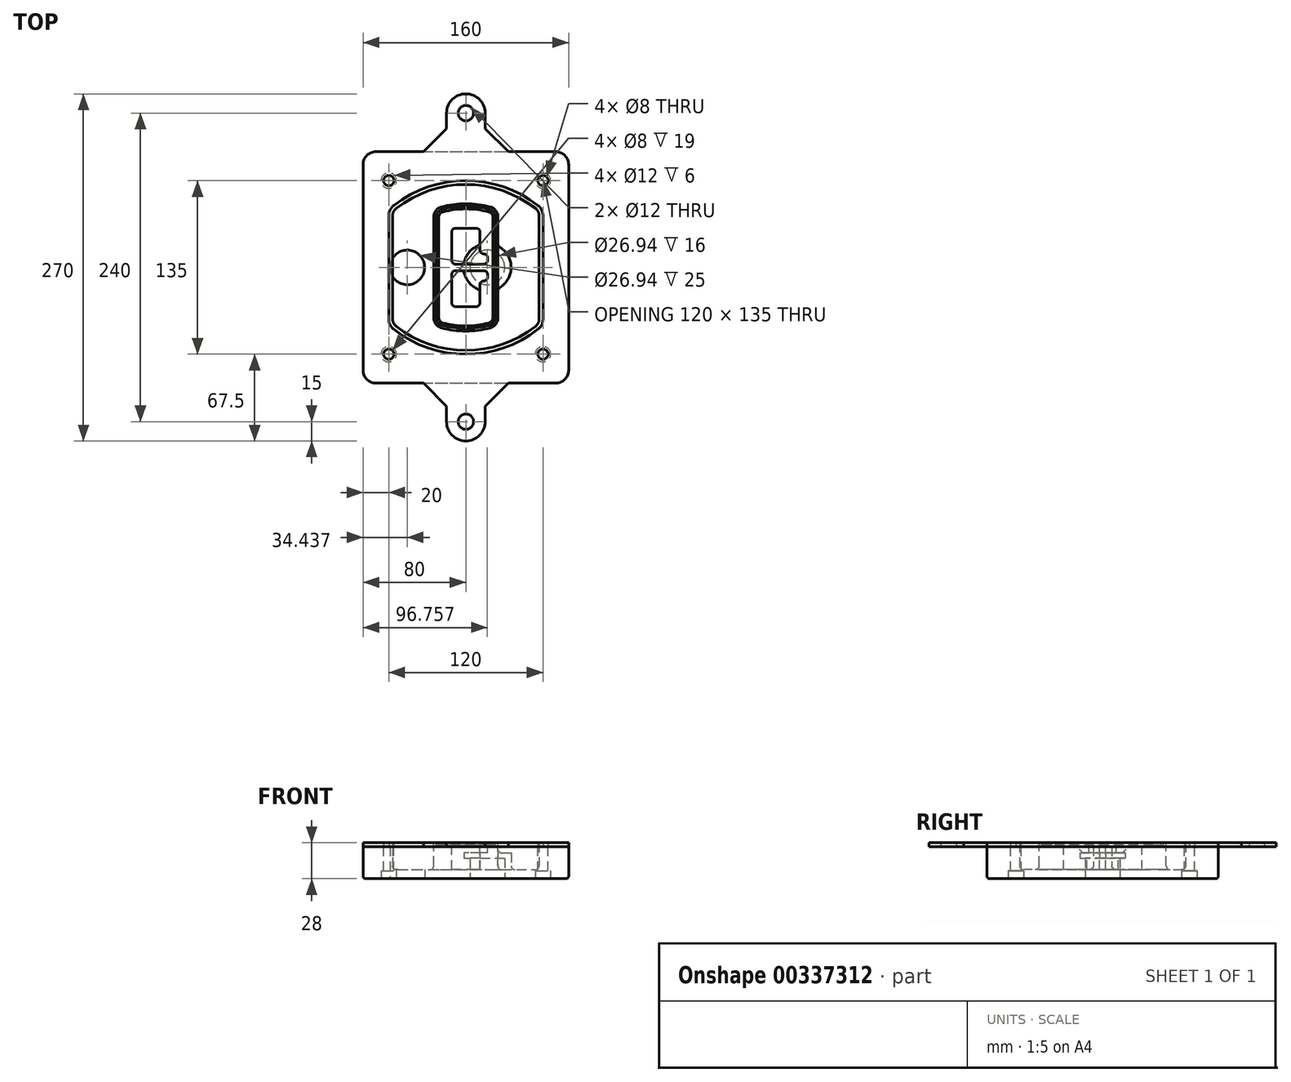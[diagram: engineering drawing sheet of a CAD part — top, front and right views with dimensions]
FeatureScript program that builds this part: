
annotation { "Feature Type Name" : "Feature", "Feature Type Description" : "" }
export const myFeature = defineFeature(function(context is Context, id is Id, definition is map)
    precondition{}
    {
        {
            var Q0;
            Q0=qCreatedBy(makeId("Top.planeOp"),FACE);
            var sketch = newSketch(context, id + "F0", { "sketchPlane" : qUnion([Q0])});
            skPoint(sketch, "E0.rect.middle", {"position": v(0, 0) * mm});
            skLineSegment(sketch, "E1.bottom", {"start": v(-70, -90) * mm, "end": v(70, -90) * mm});
            skLineSegment(sketch, "E1.top", {"start": v(-70, 90) * mm, "end": v(70, 90) * mm});
            skLineSegment(sketch, "E1.left", {"start": v(-80, -80) * mm, "end": v(-80, 80) * mm});
            skLineSegment(sketch, "E1.right", {"start": v(80, -80) * mm, "end": v(80, 80) * mm});
            skLineSegment(sketch, "E2", {"start": v(-80, 90) * mm, "end": v(80, -90) * mm, "construction": true});
            skLineSegment(sketch, "E3", {"start": v(80, 90) * mm, "end": v(-80, -90) * mm, "construction": true});
            skCircle(sketch, "E4", {"center": v(-60, 67.5) * mm, "radius": 4 * mm});
            skCircle(sketch, "E5", {"center": v(60, 67.5) * mm, "radius": 4 * mm});
            skCircle(sketch, "E6", {"center": v(60, -67.5) * mm, "radius": 4 * mm});
            skCircle(sketch, "E7", {"center": v(-60, -67.5) * mm, "radius": 4 * mm});
            skLineSegment(sketch, "E8", {"start": v(-60, 67.5) * mm, "end": v(60, 67.5) * mm, "construction": true});
            skLineSegment(sketch, "E9", {"start": v(60, 67.5) * mm, "end": v(60, -67.5) * mm, "construction": true});
            skLineSegment(sketch, "E10", {"start": v(60, -67.5) * mm, "end": v(-60, -67.5) * mm, "construction": true});
            skLineSegment(sketch, "E11", {"start": v(-60, -67.5) * mm, "end": v(-60, 67.5) * mm, "construction": true});
            skLineSegment(sketch, "E12", {"start": v(-60, 40.3) * mm, "end": v(-60, -40.3) * mm});
            skLineSegment(sketch, "E13", {"start": v(60, 40.3) * mm, "end": v(60, -40.3) * mm});
            skArc(sketch, "E14", {"start": v(56.15, 48.18) * mm, "mid": v(0, 67.5) * mm, "end": v(-56.15, 48.18) * mm});
            skArc(sketch, "E15", {"start": v(-56.15, -48.18) * mm, "mid": v(0, -67.5) * mm, "end": v(56.15, -48.18) * mm});
            skLineSegment(sketch, "E16", {"start": v(-60, 0) * mm, "end": v(60, 0) * mm, "construction": true});
            skPoint(sketch, "E17.visualSharp", {"position": v(-60, -45) * mm});
            skArc(sketch, "E17.filletArc", {"start": v(-60, -40.3) * mm, "mid": v(-58.99, -44.68) * mm, "end": v(-56.15, -48.18) * mm});
            skPoint(sketch, "E18.visualSharp", {"position": v(-60, 45) * mm});
            skArc(sketch, "E18.filletArc", {"start": v(-56.15, 48.18) * mm, "mid": v(-58.99, 44.68) * mm, "end": v(-60, 40.3) * mm});
            skPoint(sketch, "E19.visualSharp", {"position": v(60, 45) * mm});
            skArc(sketch, "E19.filletArc", {"start": v(60, 40.3) * mm, "mid": v(58.99, 44.68) * mm, "end": v(56.15, 48.18) * mm});
            skPoint(sketch, "E20.visualSharp", {"position": v(60, -45) * mm});
            skArc(sketch, "E20.filletArc", {"start": v(56.15, -48.18) * mm, "mid": v(58.99, -44.68) * mm, "end": v(60, -40.3) * mm});
            skPoint(sketch, "E21.visualSharp", {"position": v(-80, 90) * mm});
            skArc(sketch, "E21.filletArc", {"start": v(-70, 90) * mm, "mid": v(-77.07, 87.07) * mm, "end": v(-80, 80) * mm});
            skPoint(sketch, "E22.visualSharp", {"position": v(80, 90) * mm});
            skArc(sketch, "E22.filletArc", {"start": v(80, 80) * mm, "mid": v(77.07, 87.07) * mm, "end": v(70, 90) * mm});
            skPoint(sketch, "E23.visualSharp", {"position": v(80, -90) * mm});
            skArc(sketch, "E23.filletArc", {"start": v(70, -90) * mm, "mid": v(77.07, -87.07) * mm, "end": v(80, -80) * mm});
            skPoint(sketch, "E24.visualSharp", {"position": v(-80, -90) * mm});
            skArc(sketch, "E24.filletArc", {"start": v(-80, -80) * mm, "mid": v(-77.07, -87.07) * mm, "end": v(-70, -90) * mm});
            skArc(sketch, "E25.0", {"start": v(57, 40.3) * mm, "mid": v(56.3, 43.36) * mm, "end": v(54.3, 45.81) * mm});
            skLineSegment(sketch, "E25.1", {"start": v(57, 40.3) * mm, "end": v(57, -40.3) * mm});
            skArc(sketch, "E25.2", {"start": v(54.3, -45.81) * mm, "mid": v(56.3, -43.36) * mm, "end": v(57, -40.3) * mm});
            skArc(sketch, "E25.3", {"start": v(-54.3, -45.81) * mm, "mid": v(0, -64.5) * mm, "end": v(54.3, -45.81) * mm});
            skArc(sketch, "E25.4", {"start": v(-57, -40.3) * mm, "mid": v(-56.3, -43.36) * mm, "end": v(-54.3, -45.81) * mm});
            skArc(sketch, "E25.5", {"start": v(54.3, 45.81) * mm, "mid": v(0, 64.5) * mm, "end": v(-54.3, 45.81) * mm});
            skLineSegment(sketch, "E25.6", {"start": v(-57, 40.3) * mm, "end": v(-57, -40.3) * mm});
            skArc(sketch, "E25.7", {"start": v(-54.3, 45.81) * mm, "mid": v(-56.3, 43.36) * mm, "end": v(-57, 40.3) * mm});
            skArc(sketch, "E26.0", {"start": v(-58.62, 51.33) * mm, "mid": v(-62.58, 46.43) * mm, "end": v(-64, 40.3) * mm});
            skArc(sketch, "E26.1", {"start": v(58.62, 51.33) * mm, "mid": v(0, 71.5) * mm, "end": v(-58.62, 51.33) * mm});
            skArc(sketch, "E26.2", {"start": v(64, 40.3) * mm, "mid": v(62.58, 46.43) * mm, "end": v(58.62, 51.33) * mm});
            skLineSegment(sketch, "E26.3", {"start": v(64, 40.3) * mm, "end": v(64, -40.3) * mm});
            skArc(sketch, "E26.4", {"start": v(58.62, -51.33) * mm, "mid": v(62.58, -46.43) * mm, "end": v(64, -40.3) * mm});
            skLineSegment(sketch, "E26.5", {"start": v(-64, 40.3) * mm, "end": v(-64, -40.3) * mm});
            skArc(sketch, "E26.6", {"start": v(-58.62, -51.33) * mm, "mid": v(0, -71.5) * mm, "end": v(58.62, -51.33) * mm});
            skArc(sketch, "E26.7", {"start": v(-64, -40.3) * mm, "mid": v(-62.58, -46.43) * mm, "end": v(-58.62, -51.33) * mm});
            skSolve(sketch);
        }
        {
            var Q0;
            Q0=makeQuery(id+"F0.imprint","IMPRINT",FACE,{"disambiguationData":[TD([[makeQuery(id+"F0.imprint","IMPRINT",EDGE,{"derivedFrom":sQuery(id+"F0.wireOp",EDGE,"E1.bottom")}),1.0]])]});
            var Q1;
            Q1=makeQuery(id+"F0.imprint","IMPRINT",FACE,{"disambiguationData":[TD([[makeQuery(id+"F0.imprint","IMPRINT",EDGE,{"derivedFrom":sQuery(id+"F0.wireOp",EDGE,"E12")}),1.0]])]});
            var Q2;
            Q2=makeQuery(id+"F0.imprint","IMPRINT",FACE,{"disambiguationData":[TD([[makeQuery(id+"F0.imprint","IMPRINT",EDGE,{"derivedFrom":sQuery(id+"F0.wireOp",EDGE,"E25.0")}),1.0]])]});
            var Q3;
            Q3=makeQuery(id+"F0.imprint","IMPRINT",FACE,{"disambiguationData":[TD([[makeQuery(id+"F0.imprint","IMPRINT",EDGE,{"derivedFrom":sQuery(id+"F0.wireOp",EDGE,"E12")}),-1.0]])]});
            extrude(context, id + "F1", {"entities" : qUnion([Q0, Q1, Q2, Q3]), "oppositeDirection" : true, "depth" : 25 * mm});
        }
        {
            var Q0;
            Q0=makeQuery(id+"F0.imprint","IMPRINT",FACE,{"disambiguationData":[TD([[makeQuery(id+"F0.imprint","IMPRINT",EDGE,{"derivedFrom":sQuery(id+"F0.wireOp",EDGE,"E12")}),1.0]])]});
            extrude(context, id + "F2", {"entities" : qUnion([Q0]), "operationType" : NewBodyOperationType.ADD, "depth" : 3 * mm});
        }
        {
            var Q0;
            Q0=makeQuery(id+"F0.imprint","IMPRINT",FACE,{"disambiguationData":[TD([[makeQuery(id+"F0.imprint","IMPRINT",EDGE,{"derivedFrom":sQuery(id+"F0.wireOp",EDGE,"E25.0")}),1.0]])]});
            extrude(context, id + "F3", {"entities" : qUnion([Q0]), "operationType" : NewBodyOperationType.REMOVE, "oppositeDirection" : true, "depth" : 18 * mm});
        }
        {
            var Q0;
            Q0=makeQuery(id+"F2.opExtrude","CAP_FACE",FACE,{"disambiguationData":[OSD([sQuery(id+"F0.wireOp",EDGE,"E12"),sQuery(id+"F0.wireOp",EDGE,"E13"),sQuery(id+"F0.wireOp",EDGE,"E14"),sQuery(id+"F0.wireOp",EDGE,"E15"),sQuery(id+"F0.wireOp",EDGE,"E17.filletArc"),sQuery(id+"F0.wireOp",EDGE,"E18.filletArc"),sQuery(id+"F0.wireOp",EDGE,"E19.filletArc"),sQuery(id+"F0.wireOp",EDGE,"E20.filletArc"),sQuery(id+"F0.wireOp",EDGE,"E25.0"),sQuery(id+"F0.wireOp",EDGE,"E25.1"),sQuery(id+"F0.wireOp",EDGE,"E25.2"),sQuery(id+"F0.wireOp",EDGE,"E25.3"),sQuery(id+"F0.wireOp",EDGE,"E25.4"),sQuery(id+"F0.wireOp",EDGE,"E25.5"),sQuery(id+"F0.wireOp",EDGE,"E25.6"),sQuery(id+"F0.wireOp",EDGE,"E25.7")])],"isStart":false});
            var sketch = newSketch(context, id + "F4", { "sketchPlane" : qUnion([Q0])});
            skArc(sketch, "E27.0", {"start": v(-19.08, -46.97) * mm, "mid": v(0, -49.5) * mm, "end": v(19.08, -46.97) * mm});
            skArc(sketch, "E28.0", {"start": v(19.08, 46.97) * mm, "mid": v(0, 49.5) * mm, "end": v(-19.08, 46.97) * mm});
            skLineSegment(sketch, "E29", {"start": v(-25, 39.25) * mm, "end": v(-25, -39.25) * mm});
            skLineSegment(sketch, "E30", {"start": v(25, 39.25) * mm, "end": v(25, -39.25) * mm});
            skLineSegment(sketch, "E31", {"start": v(-25, 45.1) * mm, "end": v(25, 45.1) * mm, "construction": true});
            skLineSegment(sketch, "E32", {"start": v(-25, -45.1) * mm, "end": v(25, -45.1) * mm, "construction": true});
            skPoint(sketch, "E33.visualSharp", {"position": v(-25, 45.1) * mm});
            skArc(sketch, "E33.filletArc", {"start": v(-19.08, 46.97) * mm, "mid": v(-23.35, 44.11) * mm, "end": v(-25, 39.25) * mm});
            skPoint(sketch, "E34.visualSharp", {"position": v(25, 45.1) * mm});
            skArc(sketch, "E34.filletArc", {"start": v(25, 39.25) * mm, "mid": v(23.35, 44.11) * mm, "end": v(19.08, 46.97) * mm});
            skPoint(sketch, "E35.visualSharp", {"position": v(25, -45.1) * mm});
            skArc(sketch, "E35.filletArc", {"start": v(19.08, -46.97) * mm, "mid": v(23.35, -44.11) * mm, "end": v(25, -39.25) * mm});
            skPoint(sketch, "E36.visualSharp", {"position": v(-25, -45.1) * mm});
            skArc(sketch, "E36.filletArc", {"start": v(-25, -39.25) * mm, "mid": v(-23.35, -44.11) * mm, "end": v(-19.08, -46.97) * mm});
            skArc(sketch, "E37.0", {"start": v(54.3, 45.81) * mm, "mid": v(0, 64.5) * mm, "end": v(-54.3, 45.81) * mm});
            skArc(sketch, "E37.1", {"start": v(-54.3, 45.81) * mm, "mid": v(-56.3, 43.36) * mm, "end": v(-57, 40.3) * mm});
            skLineSegment(sketch, "E37.2", {"start": v(-57, 40.3) * mm, "end": v(-57, -40.3) * mm});
            skArc(sketch, "E37.3", {"start": v(-57, -40.3) * mm, "mid": v(-56.3, -43.36) * mm, "end": v(-54.3, -45.81) * mm});
            skArc(sketch, "E37.4", {"start": v(-54.3, -45.81) * mm, "mid": v(0, -64.5) * mm, "end": v(54.3, -45.81) * mm});
            skArc(sketch, "E37.5", {"start": v(54.3, -45.81) * mm, "mid": v(56.3, -43.36) * mm, "end": v(57, -40.3) * mm});
            skLineSegment(sketch, "E37.6", {"start": v(57, 40.3) * mm, "end": v(57, -40.3) * mm});
            skArc(sketch, "E37.7", {"start": v(57, 40.3) * mm, "mid": v(56.3, 43.36) * mm, "end": v(54.3, 45.81) * mm});
            skLineSegment(sketch, "E38.0", {"start": v(23, 39.25) * mm, "end": v(23, -39.25) * mm});
            skArc(sketch, "E38.1", {"start": v(18.56, -45.04) * mm, "mid": v(21.76, -42.9) * mm, "end": v(23, -39.25) * mm});
            skArc(sketch, "E38.2", {"start": v(-18.56, -45.04) * mm, "mid": v(0, -47.5) * mm, "end": v(18.56, -45.04) * mm});
            skArc(sketch, "E38.3", {"start": v(-23, -39.25) * mm, "mid": v(-21.76, -42.9) * mm, "end": v(-18.56, -45.04) * mm});
            skLineSegment(sketch, "E38.4", {"start": v(-23, 39.25) * mm, "end": v(-23, -39.25) * mm});
            skArc(sketch, "E38.5", {"start": v(23, 39.25) * mm, "mid": v(21.76, 42.9) * mm, "end": v(18.56, 45.04) * mm});
            skArc(sketch, "E38.6", {"start": v(-18.56, 45.04) * mm, "mid": v(-21.76, 42.9) * mm, "end": v(-23, 39.25) * mm});
            skArc(sketch, "E38.7", {"start": v(18.56, 45.04) * mm, "mid": v(0, 47.5) * mm, "end": v(-18.56, 45.04) * mm});
            skArc(sketch, "E39.0", {"start": v(21, 39.25) * mm, "mid": v(20.18, 41.68) * mm, "end": v(18.04, 43.1) * mm});
            skLineSegment(sketch, "E39.1", {"start": v(21, 39.25) * mm, "end": v(21, -39.25) * mm});
            skArc(sketch, "E39.2", {"start": v(18.04, -43.1) * mm, "mid": v(20.18, -41.68) * mm, "end": v(21, -39.25) * mm});
            skArc(sketch, "E39.3", {"start": v(-18.04, -43.1) * mm, "mid": v(0, -45.5) * mm, "end": v(18.04, -43.1) * mm});
            skArc(sketch, "E39.4", {"start": v(-21, -39.25) * mm, "mid": v(-20.18, -41.68) * mm, "end": v(-18.04, -43.1) * mm});
            skArc(sketch, "E39.5", {"start": v(18.04, 43.1) * mm, "mid": v(0, 45.5) * mm, "end": v(-18.04, 43.1) * mm});
            skLineSegment(sketch, "E39.6", {"start": v(-21, 39.25) * mm, "end": v(-21, -39.25) * mm});
            skArc(sketch, "E39.7", {"start": v(-18.04, 43.1) * mm, "mid": v(-20.18, 41.68) * mm, "end": v(-21, 39.25) * mm});
            skLineSegment(sketch, "E40", {"start": v(-25, 0) * mm, "end": v(25, 0) * mm, "construction": true});
            skLineSegment(sketch, "E41", {"start": v(-11, 5.5) * mm, "end": v(-11, 27.5) * mm});
            skLineSegment(sketch, "E42", {"start": v(-8, 30.5) * mm, "end": v(8, 30.5) * mm});
            skLineSegment(sketch, "E43", {"start": v(11, 27.5) * mm, "end": v(11, 13.5) * mm});
            skLineSegment(sketch, "E44", {"start": v(14, 10.5) * mm, "end": v(14, 10.5) * mm});
            skLineSegment(sketch, "E45", {"start": v(17, 7.5) * mm, "end": v(17, 5.5) * mm});
            skLineSegment(sketch, "E46", {"start": v(14, 2.5) * mm, "end": v(-8, 2.5) * mm});
            skPoint(sketch, "E47.visualSharp", {"position": v(-11, 30.5) * mm});
            skArc(sketch, "E47.filletArc", {"start": v(-8, 30.5) * mm, "mid": v(-10.12, 29.62) * mm, "end": v(-11, 27.5) * mm});
            skPoint(sketch, "E48.visualSharp", {"position": v(11, 30.5) * mm});
            skArc(sketch, "E48.filletArc", {"start": v(11, 27.5) * mm, "mid": v(10.12, 29.62) * mm, "end": v(8, 30.5) * mm});
            skPoint(sketch, "E49.visualSharp", {"position": v(11, 10.5) * mm});
            skArc(sketch, "E49.filletArc", {"start": v(11, 13.5) * mm, "mid": v(11.88, 11.38) * mm, "end": v(14, 10.5) * mm});
            skPoint(sketch, "E50.visualSharp", {"position": v(17, 10.5) * mm});
            skArc(sketch, "E50.filletArc", {"start": v(17, 7.5) * mm, "mid": v(16.12, 9.62) * mm, "end": v(14, 10.5) * mm});
            skPoint(sketch, "E51.visualSharp", {"position": v(17, 2.5) * mm});
            skArc(sketch, "E51.filletArc", {"start": v(14, 2.5) * mm, "mid": v(16.12, 3.38) * mm, "end": v(17, 5.5) * mm});
            skPoint(sketch, "E52.visualSharp", {"position": v(-11, 2.5) * mm});
            skArc(sketch, "E52.filletArc", {"start": v(-11, 5.5) * mm, "mid": v(-10.12, 3.38) * mm, "end": v(-8, 2.5) * mm});
            skLineSegment(sketch, "E53.0.MirrorCS", {"start": v(14, -2.5) * mm, "end": v(-8, -2.5) * mm});
            skArc(sketch, "E54.0.MirrorCS", {"start": v(-11, -5.5) * mm, "mid": v(-10.12, -3.38) * mm, "end": v(-8, -2.5) * mm});
            skLineSegment(sketch, "E55.0.MirrorCS", {"start": v(-11, -5.5) * mm, "end": v(-11, -27.5) * mm});
            skArc(sketch, "E56.0.MirrorCS", {"start": v(-8, -30.5) * mm, "mid": v(-10.12, -29.62) * mm, "end": v(-11, -27.5) * mm});
            skLineSegment(sketch, "E57.0.MirrorCS", {"start": v(-8, -30.5) * mm, "end": v(8, -30.5) * mm});
            skArc(sketch, "E58.0.MirrorCS", {"start": v(11, -27.5) * mm, "mid": v(10.12, -29.62) * mm, "end": v(8, -30.5) * mm});
            skLineSegment(sketch, "E59.0.MirrorCS", {"start": v(11, -27.5) * mm, "end": v(11, -13.5) * mm});
            skArc(sketch, "E60.0.MirrorCS", {"start": v(11, -13.5) * mm, "mid": v(11.88, -11.38) * mm, "end": v(14, -10.5) * mm});
            skArc(sketch, "E61.0.MirrorCS", {"start": v(17, -7.5) * mm, "mid": v(16.12, -9.62) * mm, "end": v(14, -10.5) * mm});
            skLineSegment(sketch, "E62.0.MirrorCS", {"start": v(17, -7.5) * mm, "end": v(17, -5.5) * mm});
            skArc(sketch, "E63.0.MirrorCS", {"start": v(14, -2.5) * mm, "mid": v(16.12, -3.38) * mm, "end": v(17, -5.5) * mm});
            skSolve(sketch);
        }
        {
            var Q0;
            Q0=makeQuery(id+"F4.imprint","IMPRINT",FACE,{"disambiguationData":[TD([[makeQuery(id+"F4.imprint","IMPRINT",EDGE,{"derivedFrom":sQuery(id+"F4.wireOp",EDGE,"E27.0")}),1.0]])]});
            var Q1;
            Q1=makeQuery(id+"F4.imprint","IMPRINT",FACE,{"disambiguationData":[TD([[makeQuery(id+"F4.imprint","IMPRINT",EDGE,{"derivedFrom":sQuery(id+"F4.wireOp",EDGE,"E38.0")}),-1.0]])]});
            var Q2;
            Q2=makeQuery(id+"F4.imprint","IMPRINT",FACE,{"disambiguationData":[TD([[makeQuery(id+"F4.imprint","IMPRINT",EDGE,{"derivedFrom":sQuery(id+"F4.wireOp",EDGE,"E39.0")}),1.0]])]});
            extrude(context, id + "F5", {"entities" : qUnion([Q0, Q1, Q2]), "operationType" : NewBodyOperationType.ADD, "endBound" : BoundingType.UP_TO_NEXT, "oppositeDirection" : true, "depth" : 25 * mm});
        }
        {
            var Q0;
            Q0=makeQuery(id+"F4.imprint","IMPRINT",FACE,{"disambiguationData":[TD([[makeQuery(id+"F4.imprint","IMPRINT",EDGE,{"derivedFrom":sQuery(id+"F4.wireOp",EDGE,"E38.0")}),-1.0]])]});
            extrude(context, id + "F6", {"entities" : qUnion([Q0]), "operationType" : NewBodyOperationType.REMOVE, "oppositeDirection" : true, "depth" : 2 * mm});
        }
        {
            var Q0;
            Q0=makeQuery(id+"F1.opExtrude","CAP_FACE",FACE,{"disambiguationData":[OSD([sQuery(id+"F0.wireOp",EDGE,"E1.bottom"),sQuery(id+"F0.wireOp",EDGE,"E1.top"),sQuery(id+"F0.wireOp",EDGE,"E1.left"),sQuery(id+"F0.wireOp",EDGE,"E1.right"),sQuery(id+"F0.wireOp",EDGE,"E4"),sQuery(id+"F0.wireOp",EDGE,"E5"),sQuery(id+"F0.wireOp",EDGE,"E6"),sQuery(id+"F0.wireOp",EDGE,"E7"),sQuery(id+"F0.wireOp",EDGE,"E21.filletArc"),sQuery(id+"F0.wireOp",EDGE,"E22.filletArc"),sQuery(id+"F0.wireOp",EDGE,"E23.filletArc"),sQuery(id+"F0.wireOp",EDGE,"E24.filletArc")])],"isStart":false});
            var sketch = newSketch(context, id + "F7", { "sketchPlane" : qUnion([Q0])});
            skCircle(sketch, "E64", {"center": v(16.76, 0) * mm, "radius": 13.47 * mm});
            skCircle(sketch, "E65", {"center": v(-45.56, 0) * mm, "radius": 13.47 * mm});
            skLineSegment(sketch, "E66", {"start": v(80, 0) * mm, "end": v(-80, 0) * mm});
            skCircle(sketch, "E67", {"center": v(16.76, 0) * mm, "radius": 18.47 * mm});
            skCircle(sketch, "E68", {"center": v(60, -67.5) * mm, "radius": 6 * mm});
            skCircle(sketch, "E69", {"center": v(-60, -67.5) * mm, "radius": 6 * mm});
            skCircle(sketch, "E70", {"center": v(-60, 67.5) * mm, "radius": 6 * mm});
            skCircle(sketch, "E71", {"center": v(60, 67.5) * mm, "radius": 6 * mm});
            skSolve(sketch);
        }
        {
            var Q0;
            {var subQ1=sQuery(id+"F7.wireOp",EDGE,"E66");var subQ4=sQuery(id+"F7.wireOp",EDGE,"E64");var subQ6=makeQuery(id+"F7.imprint","INTERSECT",VERTEX,{"disambiguationData":[OD(0.0)],"derivedFrom":[subQ4,subQ1]});Q0=makeQuery(id+"F7.imprint","IMPRINT",FACE,{"disambiguationData":[TD([[makeQuery(id+"F7.imprint","IMPRINT",EDGE,{"disambiguationData":[TD([[subQ6,-1.0]])],"derivedFrom":subQ4}),-1.0]])]});}
            var Q1;
            {var subQ0=sQuery(id+"F7.wireOp",EDGE,"E66");var subQ1=sQuery(id+"F7.wireOp",EDGE,"E64");var subQ3=makeQuery(id+"F7.imprint","INTERSECT",VERTEX,{"disambiguationData":[OD(0.0)],"derivedFrom":[subQ1,subQ0]});Q1=makeQuery(id+"F7.imprint","IMPRINT",FACE,{"disambiguationData":[TD([[makeQuery(id+"F7.imprint","IMPRINT",EDGE,{"disambiguationData":[TD([[subQ3,-1.0]])],"derivedFrom":subQ1}),1.0]])]});}
            var Q2;
            {var subQ0=sQuery(id+"F7.wireOp",EDGE,"E66");var subQ1=sQuery(id+"F7.wireOp",EDGE,"E64");var subQ3=makeQuery(id+"F7.imprint","INTERSECT",VERTEX,{"disambiguationData":[OD(0.0)],"derivedFrom":[subQ1,subQ0]});Q2=makeQuery(id+"F7.imprint","IMPRINT",FACE,{"disambiguationData":[TD([[makeQuery(id+"F7.imprint","IMPRINT",EDGE,{"disambiguationData":[TD([[subQ3,1.0]])],"derivedFrom":subQ1}),1.0]])]});}
            var Q3;
            {var subQ1=sQuery(id+"F7.wireOp",EDGE,"E66");var subQ4=sQuery(id+"F7.wireOp",EDGE,"E64");var subQ6=makeQuery(id+"F7.imprint","INTERSECT",VERTEX,{"disambiguationData":[OD(0.0)],"derivedFrom":[subQ4,subQ1]});Q3=makeQuery(id+"F7.imprint","IMPRINT",FACE,{"disambiguationData":[TD([[makeQuery(id+"F7.imprint","IMPRINT",EDGE,{"disambiguationData":[TD([[subQ6,1.0]])],"derivedFrom":subQ4}),-1.0]])]});}
            extrude(context, id + "F8", {"entities" : qUnion([Q0, Q1, Q2, Q3]), "operationType" : NewBodyOperationType.ADD, "oppositeDirection" : true, "depth" : 20 * mm});
        }
        {
            var Q0;
            {var subQ0=sQuery(id+"F7.wireOp",EDGE,"E66");var subQ1=sQuery(id+"F7.wireOp",EDGE,"E64");var subQ3=makeQuery(id+"F7.imprint","INTERSECT",VERTEX,{"disambiguationData":[OD(0.0)],"derivedFrom":[subQ1,subQ0]});Q0=makeQuery(id+"F7.imprint","IMPRINT",FACE,{"disambiguationData":[TD([[makeQuery(id+"F7.imprint","IMPRINT",EDGE,{"disambiguationData":[TD([[subQ3,-1.0]])],"derivedFrom":subQ1}),1.0]])]});}
            var Q1;
            {var subQ0=sQuery(id+"F7.wireOp",EDGE,"E66");var subQ1=sQuery(id+"F7.wireOp",EDGE,"E64");var subQ3=makeQuery(id+"F7.imprint","INTERSECT",VERTEX,{"disambiguationData":[OD(0.0)],"derivedFrom":[subQ1,subQ0]});Q1=makeQuery(id+"F7.imprint","IMPRINT",FACE,{"disambiguationData":[TD([[makeQuery(id+"F7.imprint","IMPRINT",EDGE,{"disambiguationData":[TD([[subQ3,1.0]])],"derivedFrom":subQ1}),1.0]])]});}
            extrude(context, id + "F9", {"entities" : qUnion([Q0, Q1]), "operationType" : NewBodyOperationType.REMOVE, "oppositeDirection" : true, "depth" : 16 * mm});
        }
        {
            var Q0;
            {var subQ0=sQuery(id+"F7.wireOp",EDGE,"E66");var subQ1=sQuery(id+"F7.wireOp",EDGE,"E65");var subQ3=makeQuery(id+"F7.imprint","INTERSECT",VERTEX,{"disambiguationData":[OD(0.0)],"derivedFrom":[subQ1,subQ0]});Q0=makeQuery(id+"F7.imprint","IMPRINT",FACE,{"disambiguationData":[TD([[makeQuery(id+"F7.imprint","IMPRINT",EDGE,{"disambiguationData":[TD([[subQ3,-1.0]])],"derivedFrom":subQ1}),1.0]])]});}
            var Q1;
            {var subQ0=sQuery(id+"F7.wireOp",EDGE,"E66");var subQ1=sQuery(id+"F7.wireOp",EDGE,"E65");var subQ3=makeQuery(id+"F7.imprint","INTERSECT",VERTEX,{"disambiguationData":[OD(0.0)],"derivedFrom":[subQ1,subQ0]});Q1=makeQuery(id+"F7.imprint","IMPRINT",FACE,{"disambiguationData":[TD([[makeQuery(id+"F7.imprint","IMPRINT",EDGE,{"disambiguationData":[TD([[subQ3,1.0]])],"derivedFrom":subQ1}),1.0]])]});}
            extrude(context, id + "F10", {"entities" : qUnion([Q0, Q1]), "operationType" : NewBodyOperationType.REMOVE, "oppositeDirection" : true, "depth" : 25 * mm});
        }
        {
            var Q0;
            Q0=makeQuery(id+"F7.imprint","IMPRINT",FACE,{"disambiguationData":[TD([[makeQuery(id+"F7.imprint","IMPRINT",EDGE,{"derivedFrom":sQuery(id+"F7.wireOp",EDGE,"E68")}),1.0]])]});
            var Q1;
            Q1=makeQuery(id+"F7.imprint","IMPRINT",FACE,{"disambiguationData":[TD([[makeQuery(id+"F7.imprint","IMPRINT",EDGE,{"derivedFrom":makeQuery(id+"F1.opExtrude","CAP_EDGE",EDGE,{"disambiguationData":[OSD([sQuery(id+"F0.wireOp",EDGE,"E5")])],"isStart":false})}),-1.0]])]});
            var Q2;
            Q2=makeQuery(id+"F7.imprint","IMPRINT",FACE,{"disambiguationData":[TD([[makeQuery(id+"F7.imprint","IMPRINT",EDGE,{"derivedFrom":sQuery(id+"F7.wireOp",EDGE,"E69")}),1.0]])]});
            var Q3;
            Q3=makeQuery(id+"F7.imprint","IMPRINT",FACE,{"disambiguationData":[TD([[makeQuery(id+"F7.imprint","IMPRINT",EDGE,{"derivedFrom":makeQuery(id+"F1.opExtrude","CAP_EDGE",EDGE,{"disambiguationData":[OSD([sQuery(id+"F0.wireOp",EDGE,"E4")])],"isStart":false})}),-1.0]])]});
            var Q4;
            Q4=makeQuery(id+"F7.imprint","IMPRINT",FACE,{"disambiguationData":[TD([[makeQuery(id+"F7.imprint","IMPRINT",EDGE,{"derivedFrom":sQuery(id+"F7.wireOp",EDGE,"E70")}),1.0]])]});
            var Q5;
            Q5=makeQuery(id+"F7.imprint","IMPRINT",FACE,{"disambiguationData":[TD([[makeQuery(id+"F7.imprint","IMPRINT",EDGE,{"derivedFrom":makeQuery(id+"F1.opExtrude","CAP_EDGE",EDGE,{"disambiguationData":[OSD([sQuery(id+"F0.wireOp",EDGE,"E7")])],"isStart":false})}),-1.0]])]});
            var Q6;
            Q6=makeQuery(id+"F7.imprint","IMPRINT",FACE,{"disambiguationData":[TD([[makeQuery(id+"F7.imprint","IMPRINT",EDGE,{"derivedFrom":sQuery(id+"F7.wireOp",EDGE,"E71")}),1.0]])]});
            var Q7;
            Q7=makeQuery(id+"F7.imprint","IMPRINT",FACE,{"disambiguationData":[TD([[makeQuery(id+"F7.imprint","IMPRINT",EDGE,{"derivedFrom":makeQuery(id+"F1.opExtrude","CAP_EDGE",EDGE,{"disambiguationData":[OSD([sQuery(id+"F0.wireOp",EDGE,"E6")])],"isStart":false})}),-1.0]])]});
            extrude(context, id + "F11", {"entities" : qUnion([Q0, Q1, Q2, Q3, Q4, Q5, Q6, Q7]), "operationType" : NewBodyOperationType.REMOVE, "oppositeDirection" : true, "depth" : 6 * mm});
        }
        {
            var Q0;
            Q0=makeQuery(id+"F9.boolean.opBoolean","COPY",FACE,{"derivedFrom":makeQuery(id+"F9.opExtrude","CAP_FACE",FACE,{"disambiguationData":[OSD([sQuery(id+"F7.wireOp",EDGE,"E64")])],"isStart":false})});
            var sketch = newSketch(context, id + "F12", { "sketchPlane" : qUnion([Q0])});
            skArc(sketch, "E72.0", {"start": v(11, 17.55) * mm, "mid": v(2.57, 11.82) * mm, "end": v(-1.54, 2.5) * mm});
            skArc(sketch, "E72.1", {"start": v(-1.54, -2.5) * mm, "mid": v(2.57, -11.82) * mm, "end": v(11, -17.55) * mm});
            skLineSegment(sketch, "E73", {"start": v(-1.54, -2.5) * mm, "end": v(14, -2.5) * mm});
            skLineSegment(sketch, "E74.0", {"start": v(14, 2.5) * mm, "end": v(-1.54, 2.5) * mm});
            skArc(sketch, "E74.1", {"start": v(14, 2.5) * mm, "mid": v(16.12, 3.38) * mm, "end": v(17, 5.5) * mm});
            skLineSegment(sketch, "E74.2", {"start": v(17, 7.5) * mm, "end": v(17, 5.5) * mm});
            skArc(sketch, "E74.3", {"start": v(17, 7.5) * mm, "mid": v(16.12, 9.62) * mm, "end": v(14, 10.5) * mm});
            skArc(sketch, "E74.4", {"start": v(11, 13.5) * mm, "mid": v(11.88, 11.38) * mm, "end": v(14, 10.5) * mm});
            skLineSegment(sketch, "E74.5", {"start": v(11, 17.55) * mm, "end": v(11, 13.5) * mm});
            skLineSegment(sketch, "E74.7", {"start": v(14, -2.5) * mm, "end": v(-1.54, -2.5) * mm});
            skArc(sketch, "E74.8", {"start": v(14, -2.5) * mm, "mid": v(16.12, -3.38) * mm, "end": v(17, -5.5) * mm});
            skLineSegment(sketch, "E74.9", {"start": v(17, -7.5) * mm, "end": v(17, -5.5) * mm});
            skArc(sketch, "E74.10", {"start": v(17, -7.5) * mm, "mid": v(16.12, -9.62) * mm, "end": v(14, -10.5) * mm});
            skArc(sketch, "E74.11", {"start": v(11, -13.5) * mm, "mid": v(11.88, -11.38) * mm, "end": v(14, -10.5) * mm});
            skLineSegment(sketch, "E74.12", {"start": v(11, -17.55) * mm, "end": v(11, -13.5) * mm});
            skPoint(sketch, "E75.orphan", {"position": v(11, -27.5) * mm});
            skPoint(sketch, "E76.orphan", {"position": v(-8, -2.5) * mm});
            skPoint(sketch, "E77.orphan", {"position": v(-8, 2.5) * mm});
            skPoint(sketch, "E78.orphan", {"position": v(11, 27.5) * mm});
            skSolve(sketch);
        }
        {
            var Q0;
            {var subQ7=sQuery(id+"F12.wireOp",EDGE,"E72.0");var subQ14=sQuery(id+"F12.wireOp",EDGE,"E72.1");var subQ16=sQuery(id+"F12.wireOp",EDGE,"E74.1");var subQ18=sQuery(id+"F12.wireOp",EDGE,"E74.8");Q0=qUnion([makeQuery(id+"F12.imprint","IMPRINT",FACE,{"disambiguationData":[TD([[makeQuery(id+"F12.imprint","IMPRINT",EDGE,{"derivedFrom":subQ7}),1.0]])]}),makeQuery(id+"F12.imprint","IMPRINT",FACE,{"disambiguationData":[TD([[makeQuery(id+"F12.imprint","IMPRINT",EDGE,{"derivedFrom":subQ14}),1.0]])]}),makeQuery(id+"F12.imprint","IMPRINT",FACE,{"disambiguationData":[TD([[makeQuery(id+"F12.imprint","IMPRINT",EDGE,{"derivedFrom":subQ16}),1.0]])]}),makeQuery(id+"F12.imprint","IMPRINT",FACE,{"disambiguationData":[TD([[makeQuery(id+"F12.imprint","IMPRINT",EDGE,{"derivedFrom":subQ18}),-1.0]])]})]);}
            var Q1;
            Q1=makeQuery(id+"F5.boolean.opBoolean","SPLIT",FACE,{"disambiguationData":[TD([makeQuery(id+"F5.opExtrude","SWEPT_FACE",FACE,{"disambiguationData":[OSD([sQuery(id+"F4.wireOp",EDGE,"E41")])]})])],"derivedFrom":makeQuery(id+"F3.boolean.opBoolean","COPY",FACE,{"derivedFrom":makeQuery(id+"F3.opExtrude","CAP_FACE",FACE,{"disambiguationData":[OSD([sQuery(id+"F0.wireOp",EDGE,"E25.0"),sQuery(id+"F0.wireOp",EDGE,"E25.1"),sQuery(id+"F0.wireOp",EDGE,"E25.2"),sQuery(id+"F0.wireOp",EDGE,"E25.3"),sQuery(id+"F0.wireOp",EDGE,"E25.4"),sQuery(id+"F0.wireOp",EDGE,"E25.5"),sQuery(id+"F0.wireOp",EDGE,"E25.6"),sQuery(id+"F0.wireOp",EDGE,"E25.7")])],"isStart":false})})});
            extrude(context, id + "F13", {"entities" : qUnion([Q0]), "operationType" : NewBodyOperationType.REMOVE, "endBound" : BoundingType.UP_TO_SURFACE, "endBoundEntityFace" : qUnion([Q1]), "depth" : 25 * mm});
        }
        {
            var Q0;
            Q0=makeQuery(id+"F3.boolean.opBoolean","COPY",EDGE,{"derivedFrom":makeQuery(id+"F3.opExtrude","CAP_EDGE",EDGE,{"disambiguationData":[OSD([sQuery(id+"F0.wireOp",EDGE,"E25.6")])],"isStart":false})});
            var Q1;
            Q1=makeQuery(id+"F8.boolean.opBoolean","INTERSECT",EDGE,{"derivedFrom":[makeQuery(id+"F5.opExtrude","SWEPT_FACE",FACE,{"disambiguationData":[OSD([sQuery(id+"F4.wireOp",EDGE,"E30")])]}),makeQuery(id+"F8.opExtrude","CAP_FACE",FACE,{"disambiguationData":[OSD([sQuery(id+"F7.wireOp",EDGE,"E67")])],"isStart":false})]});
            var Q2;
            Q2=makeQuery(id+"F8.boolean.opBoolean","INTERSECT",EDGE,{"disambiguationData":[OD(1.0)],"derivedFrom":[makeQuery(id+"F5.opExtrude","SWEPT_FACE",FACE,{"disambiguationData":[OSD([sQuery(id+"F4.wireOp",EDGE,"E30")])]}),makeQuery(id+"F8.opExtrude","SWEPT_FACE",FACE,{"disambiguationData":[OSD([sQuery(id+"F7.wireOp",EDGE,"E67")])]})]});
            var Q3;
            {var subQ0=sQuery(id+"F4.wireOp",EDGE,"E30");Q3=makeQuery(id+"F8.boolean.opBoolean","SPLIT",EDGE,{"disambiguationData":[TD([makeQuery(id+"F5.opExtrude","SWEPT_FACE",FACE,{"disambiguationData":[OSD([sQuery(id+"F4.wireOp",EDGE,"E35.filletArc")])]})])],"derivedFrom":makeQuery(id+"F5.opExtrude","CAP_EDGE",EDGE,{"disambiguationData":[OSD([subQ0])],"isStart":false})});}
            var Q4;
            {var subQ0=sQuery(id+"F0.wireOp",EDGE,"E25.7");var subQ1=sQuery(id+"F0.wireOp",EDGE,"E25.1");var subQ2=sQuery(id+"F0.wireOp",EDGE,"E25.6");var subQ3=sQuery(id+"F0.wireOp",EDGE,"E25.5");var subQ4=sQuery(id+"F0.wireOp",EDGE,"E25.4");var subQ5=sQuery(id+"F0.wireOp",EDGE,"E25.0");var subQ6=sQuery(id+"F0.wireOp",EDGE,"E25.2");var subQ7=sQuery(id+"F0.wireOp",EDGE,"E25.3");Q4=makeQuery(id+"F8.boolean.opBoolean","INTERSECT",EDGE,{"derivedFrom":[makeQuery(id+"F5.boolean.opBoolean","SPLIT",FACE,{"disambiguationData":[TD([makeQuery(id+"F2.opExtrude","SWEPT_FACE",FACE,{"disambiguationData":[OSD([subQ5])]})])],"derivedFrom":makeQuery(id+"F3.boolean.opBoolean","COPY",FACE,{"derivedFrom":makeQuery(id+"F3.opExtrude","CAP_FACE",FACE,{"disambiguationData":[OSD([subQ5,subQ1,subQ6,subQ7,subQ4,subQ3,subQ2,subQ0])],"isStart":false})})}),makeQuery(id+"F8.opExtrude","SWEPT_FACE",FACE,{"disambiguationData":[OSD([sQuery(id+"F7.wireOp",EDGE,"E67")])]})]});}
            var Q5;
            Q5=makeQuery(id+"F8.boolean.opBoolean","INTERSECT",EDGE,{"disambiguationData":[OD(0.0)],"derivedFrom":[makeQuery(id+"F5.opExtrude","SWEPT_FACE",FACE,{"disambiguationData":[OSD([sQuery(id+"F4.wireOp",EDGE,"E30")])]}),makeQuery(id+"F8.opExtrude","SWEPT_FACE",FACE,{"disambiguationData":[OSD([sQuery(id+"F7.wireOp",EDGE,"E67")])]})]});
            fillet(context, id + "F14", {"entities" : qUnion([Q0, Q1, Q2, Q3, Q4, Q5]), "radius" : 3 * mm, "tangentPropagation" : true, "allowEdgeOverflow" : false});
        }
        {
            var Q0;
            Q0=makeQuery(id+"F1.opExtrude","CAP_EDGE",EDGE,{"disambiguationData":[OSD([sQuery(id+"F0.wireOp",EDGE,"E1.bottom")])],"isStart":false});
            fillet(context, id + "F15", {"entities" : qUnion([Q0]), "radius" : 2 * mm, "tangentPropagation" : true, "allowEdgeOverflow" : false});
        }
        {
            var Q0;
            {var subQ0=sQuery(id+"F0.wireOp",EDGE,"E21.filletArc");var subQ1=sQuery(id+"F0.wireOp",EDGE,"E7");var subQ2=sQuery(id+"F0.wireOp",EDGE,"E6");var subQ3=sQuery(id+"F0.wireOp",EDGE,"E5");var subQ4=sQuery(id+"F0.wireOp",EDGE,"E4");var subQ5=sQuery(id+"F0.wireOp",EDGE,"E22.filletArc");var subQ6=sQuery(id+"F0.wireOp",EDGE,"E1.bottom");var subQ7=sQuery(id+"F0.wireOp",EDGE,"E1.right");var subQ8=sQuery(id+"F0.wireOp",EDGE,"E1.top");var subQ9=sQuery(id+"F0.wireOp",EDGE,"E1.left");var subQ10=sQuery(id+"F0.wireOp",EDGE,"E23.filletArc");var subQ11=sQuery(id+"F0.wireOp",EDGE,"E24.filletArc");Q0=makeQuery(id+"F2.boolean.opBoolean","SPLIT",FACE,{"disambiguationData":[TD([makeQuery(id+"F1.opExtrude","SWEPT_FACE",FACE,{"disambiguationData":[OSD([subQ6])]})])],"derivedFrom":makeQuery(id+"F1.opExtrude","CAP_FACE",FACE,{"disambiguationData":[OSD([subQ6,subQ8,subQ9,subQ7,subQ4,subQ3,subQ2,subQ1,subQ0,subQ5,subQ10,subQ11])],"isStart":true})});}
            var sketch = newSketch(context, id + "F16", { "sketchPlane" : qUnion([Q0])});
            skLineSegment(sketch, "E79", {"start": v(0, 90) * mm, "end": v(0, 120) * mm, "construction": true});
            skCircle(sketch, "E80", {"center": v(0, 120) * mm, "radius": 6 * mm});
            skLineSegment(sketch, "E81", {"start": v(-33, 90) * mm, "end": v(-15, 108) * mm});
            skLineSegment(sketch, "E82", {"start": v(-15, 108) * mm, "end": v(-15, 120) * mm});
            skLineSegment(sketch, "E83", {"start": v(33, 90) * mm, "end": v(15, 108) * mm});
            skLineSegment(sketch, "E84", {"start": v(15, 108) * mm, "end": v(15, 120) * mm});
            skArc(sketch, "E85", {"start": v(15, 120) * mm, "mid": v(0, 135) * mm, "end": v(-15, 120) * mm});
            skLineSegment(sketch, "E86", {"start": v(-80, 0) * mm, "end": v(80, 0) * mm, "construction": true});
            skLineSegment(sketch, "E87.MirrorCS", {"start": v(33, -90) * mm, "end": v(15, -108) * mm});
            skLineSegment(sketch, "E88.MirrorCS", {"start": v(15, -108) * mm, "end": v(15, -120) * mm});
            skArc(sketch, "E89.MirrorCS", {"start": v(15, -120) * mm, "mid": v(0, -135) * mm, "end": v(-15, -120) * mm});
            skCircle(sketch, "E90.MirrorC", {"center": v(0, -120) * mm, "radius": 6 * mm});
            skLineSegment(sketch, "E91.MirrorCS", {"start": v(0, -90) * mm, "end": v(0, -120) * mm, "construction": true});
            skLineSegment(sketch, "E92.MirrorCS", {"start": v(-33, -90) * mm, "end": v(-15, -108) * mm});
            skLineSegment(sketch, "E93.MirrorCS", {"start": v(-15, -108) * mm, "end": v(-15, -120) * mm});
            skSolve(sketch);
        }
        {
            var Q0;
            Q0=makeQuery(id+"F16.imprint","IMPRINT",FACE,{"disambiguationData":[TD([[makeQuery(id+"F16.imprint","IMPRINT",EDGE,{"derivedFrom":sQuery(id+"F16.wireOp",EDGE,"E80")}),-1.0]])]});
            var Q1;
            {var subQ0=sQuery(id+"F16.wireOp",EDGE,"E87.MirrorCS");Q1=makeQuery(id+"F16.imprint","IMPRINT",FACE,{"disambiguationData":[TD([[makeQuery(id+"F16.imprint","IMPRINT",EDGE,{"derivedFrom":subQ0}),-1.0]])]});}
            var Q2;
            Q2=makeQuery(id+"F16.imprint","IMPRINT",FACE,{"disambiguationData":[TD([[makeQuery(id+"F16.imprint","IMPRINT",EDGE,{"derivedFrom":makeQuery(id+"F1.opExtrude","CAP_EDGE",EDGE,{"disambiguationData":[OSD([sQuery(id+"F0.wireOp",EDGE,"E1.left")])],"isStart":true})}),-1.0]])]});
            var Q3;
            Q3=makeQuery(id+"F2.opExtrude","CAP_FACE",FACE,{"disambiguationData":[OSD([sQuery(id+"F0.wireOp",EDGE,"E12"),sQuery(id+"F0.wireOp",EDGE,"E13"),sQuery(id+"F0.wireOp",EDGE,"E14"),sQuery(id+"F0.wireOp",EDGE,"E15"),sQuery(id+"F0.wireOp",EDGE,"E17.filletArc"),sQuery(id+"F0.wireOp",EDGE,"E18.filletArc"),sQuery(id+"F0.wireOp",EDGE,"E19.filletArc"),sQuery(id+"F0.wireOp",EDGE,"E20.filletArc"),sQuery(id+"F0.wireOp",EDGE,"E25.0"),sQuery(id+"F0.wireOp",EDGE,"E25.1"),sQuery(id+"F0.wireOp",EDGE,"E25.2"),sQuery(id+"F0.wireOp",EDGE,"E25.3"),sQuery(id+"F0.wireOp",EDGE,"E25.4"),sQuery(id+"F0.wireOp",EDGE,"E25.5"),sQuery(id+"F0.wireOp",EDGE,"E25.6"),sQuery(id+"F0.wireOp",EDGE,"E25.7")])],"isStart":false});
            extrude(context, id + "F17", {"entities" : qUnion([Q0, Q1, Q2]), "endBound" : BoundingType.UP_TO_SURFACE, "endBoundEntityFace" : qUnion([Q3]), "depth" : 25 * mm});
        }
    });
